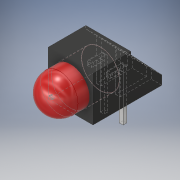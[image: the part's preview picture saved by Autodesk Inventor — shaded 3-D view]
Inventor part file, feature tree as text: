
AUTODESK INVENTOR PART (.ipt)
format: ipt  version: 2019.1 (Build 231200000, 200)  size: 276,992 bytes
history: native  units: mm
features: extrude x7, sketch x7, other x5, fillet x1, mirror x1
ambient origin geometry x8: Origin, YZ Plane, XZ Plane, XY Plane, X Axis, Y Axis, Z Axis, Center Point
bodies: Body1 (feature_tree), Body2 (feature_tree), Body3 (feature_tree)
feature tree (21):
  other  "Plastic"
  extrude  "Выдавливание1"  Depth=0.4mm
  extrude  "Выдавливание2"  Depth=6.0mm
  extrude  "Выдавливание3"  Depth=9.2mm
  extrude  "Выдавливание4"  Depth=6.0mm TaperAngle=0.0deg
  extrude  "Выдавливание5"  Depth=5.1mm
  fillet  "Сопряжение1"  Radius=4.0mm
  other  "РабПлоскость1"
  extrude  "Выдавливание6"  Depth=2.54mm
  mirror  "Зеркальное отражение1"
  extrude  "Выдавливание7"  Depth=0.6mm
  sketch  "Эскиз1"
  other  "Картинка1"
  sketch  "Эскиз2"
  sketch  "Эскиз3"
  sketch  "Эскиз5"
  sketch  "Эскиз6"
  other  "Led"
  sketch  "Эскиз8"
  other  "Led_pin"
  sketch  "Эскиз9"
